# Revit family: 32 Binnendeur - Draaiend - Recht - Vol - 1x_S
name_source: partatom
category: Doors
revit_build: Autodesk Revit Architecture 2012 (Build: 20110309_2315(x64)
units: mm (PartAtom-declared; Revit-internal decimal feet)

## types (4) — shared parameters
BE Deurblad Dikte = 40 mm  [stored 0.131234 ft]
BE Vast Kader Breedte = 40 mm  [stored 0.131234 ft]
Description = 32 Binnendeur - Draaiend - Recht - Vol - 1x_S
Function = Interior
Keynote = 40.00
Wall Closure = By host

## per-type parameters (varying)
| type | BE Deurblad Positie | BE Kader Blok | BE Kader Omlijsting | BE Stoplat Zichtbaar | BE Zwaaideur |
| Opendraaiend / Kader-Blok | 0 mm  [stored 0 ft] | Yes | No | Yes | No |
| Opendraaiend / Kader-Omlijsting | 0 mm  [stored 0 ft] | No | Yes | Yes | No |
| Zwaai / Kader-Blok | 50 mm  [stored 0.164042 ft] | Yes | No | No | Yes |
| Zwaai / Kader-Omlijsting | 50 mm  [stored 0.164042 ft] | No | Yes | No | Yes |

note: [stored X ft] marks values corroborated as IEEE doubles in the binary element streams (Revit-internal decimal feet)

## geometry (parser evidence)
native form markers: Sweep x2
no freeform markers — native parametric forms only
